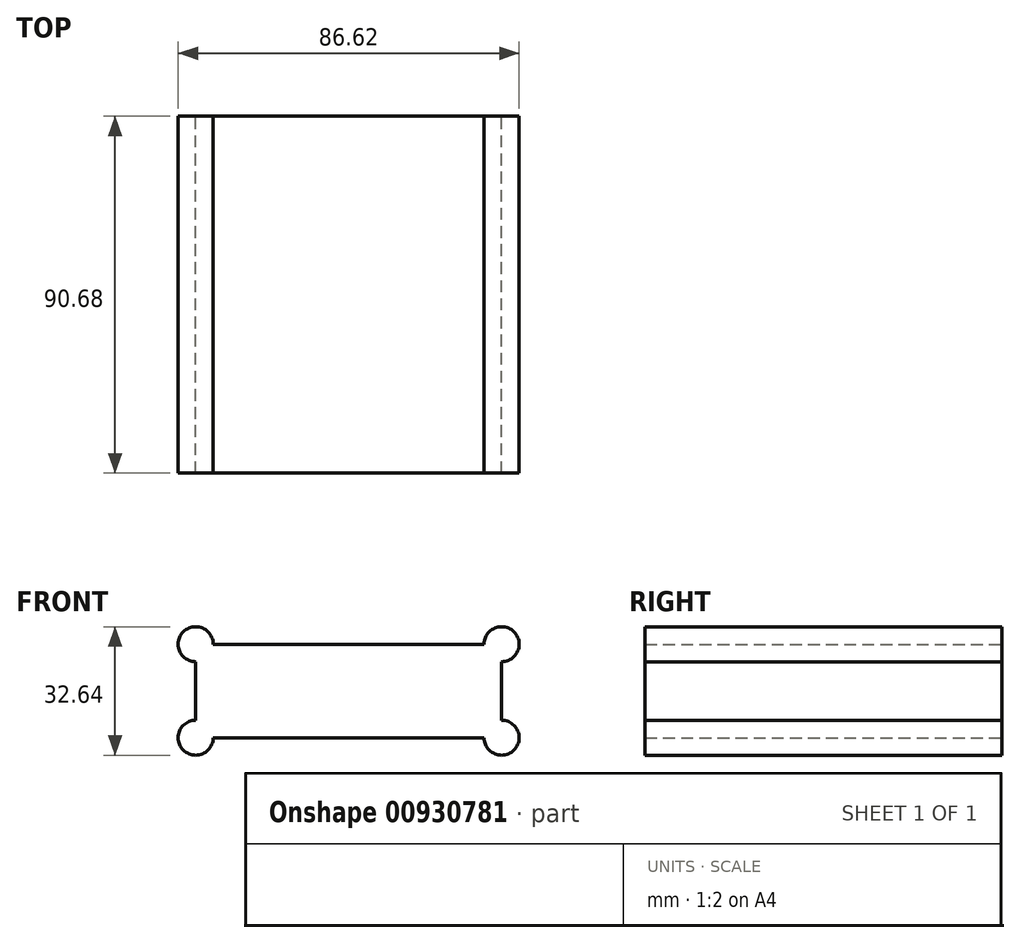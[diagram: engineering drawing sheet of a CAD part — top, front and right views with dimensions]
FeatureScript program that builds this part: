
annotation { "Feature Type Name" : "Feature", "Feature Type Description" : "" }
export const myFeature = defineFeature(function(context is Context, id is Id, definition is map)
    precondition{}
    {
        {
            var Q0;
            Q0=qCreatedBy(makeId("Front.planeOp"),FACE);
            var sketch = newSketch(context, id + "F0", { "sketchPlane" : qUnion([Q0])});
            skLineSegment(sketch, "E0.bottom", {"start": v(-38.86, 11.88) * mm, "end": v(38.86, 11.88) * mm});
            skLineSegment(sketch, "E0.top", {"start": v(-38.86, -11.88) * mm, "end": v(38.86, -11.88) * mm});
            skLineSegment(sketch, "E0.left", {"start": v(-38.86, 11.88) * mm, "end": v(-38.86, -11.88) * mm});
            skLineSegment(sketch, "E0.right", {"start": v(38.86, 11.88) * mm, "end": v(38.86, -11.88) * mm});
            skPoint(sketch, "E0.middle", {"position": v(0, 0) * mm});
            skCircle(sketch, "E1", {"center": v(38.86, 11.88) * mm, "radius": 4.45 * mm});
            skCircle(sketch, "E2", {"center": v(-38.86, 11.88) * mm, "radius": 4.45 * mm});
            skCircle(sketch, "E3", {"center": v(-38.86, -11.88) * mm, "radius": 4.45 * mm});
            skCircle(sketch, "E4", {"center": v(38.86, -11.88) * mm, "radius": 4.45 * mm});
            skSolve(sketch);
        }
        {
            var Q0;
            Q0 = qSketchRegion(id + "F0", true);
            extrude(context, id + "F1", {"entities" : qUnion([Q0]), "depth" : 90.68 * mm, "offsetDistance" : 25.4 * mm});
        }
    });
